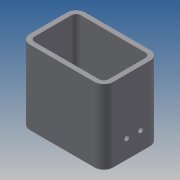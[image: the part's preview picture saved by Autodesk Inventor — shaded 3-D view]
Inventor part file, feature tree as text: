
AUTODESK INVENTOR PART (.ipt)
format: ipt  version: 2014 SP1 (Build 180222100, 222)  size: 121,344 bytes
history: native  units: in
note: dims shown in document units (in); Inventor stores cm internally (conversion verified against a paired STEP export)
features: sketch x4, extrude x2, hole x2
ambient origin geometry x8: Origin, YZ Plane, XZ Plane, XY Plane, X Axis, Y Axis, Z Axis, Center Point
bodies: Solid1 (feature_tree)
feature tree (8):
  extrude  "Extrusion1"  Depth=24.0in
  extrude  "Extrusion3"  Depth=4.0in
  hole  "Hole3"  [1 undecoded]
  hole  "Hole4"  [1 undecoded]
  sketch  "Sketch1"  dims[d0=36.0in d1=24.0in]
  sketch  "Sketch3"  dims[d2=2.0in d3=0.0in d9=4.0in]
  sketch  "Sketch6"  dims[d10=2.0in d11=30.0in d12=0.0in]
  sketch  "Sketch7"  dims[d35=24.0in d36=6.0in d37=2.1654in d38=0.75in d39=0.375in d40=0.25in d41=0.5635in d42=1.0in d43=0.8108in d44=2.5in d45=6.0in d46=2.1654in d47=0.75in d48=0.375in d49=0.25in d50=0.5635in d51=6.0in d52=0.8108in]
note: 2 required parameter values undecoded (feature->parameter linkage not recoverable at this tier; creation-order binding heuristic only, values carry confidence <= 0.55)
